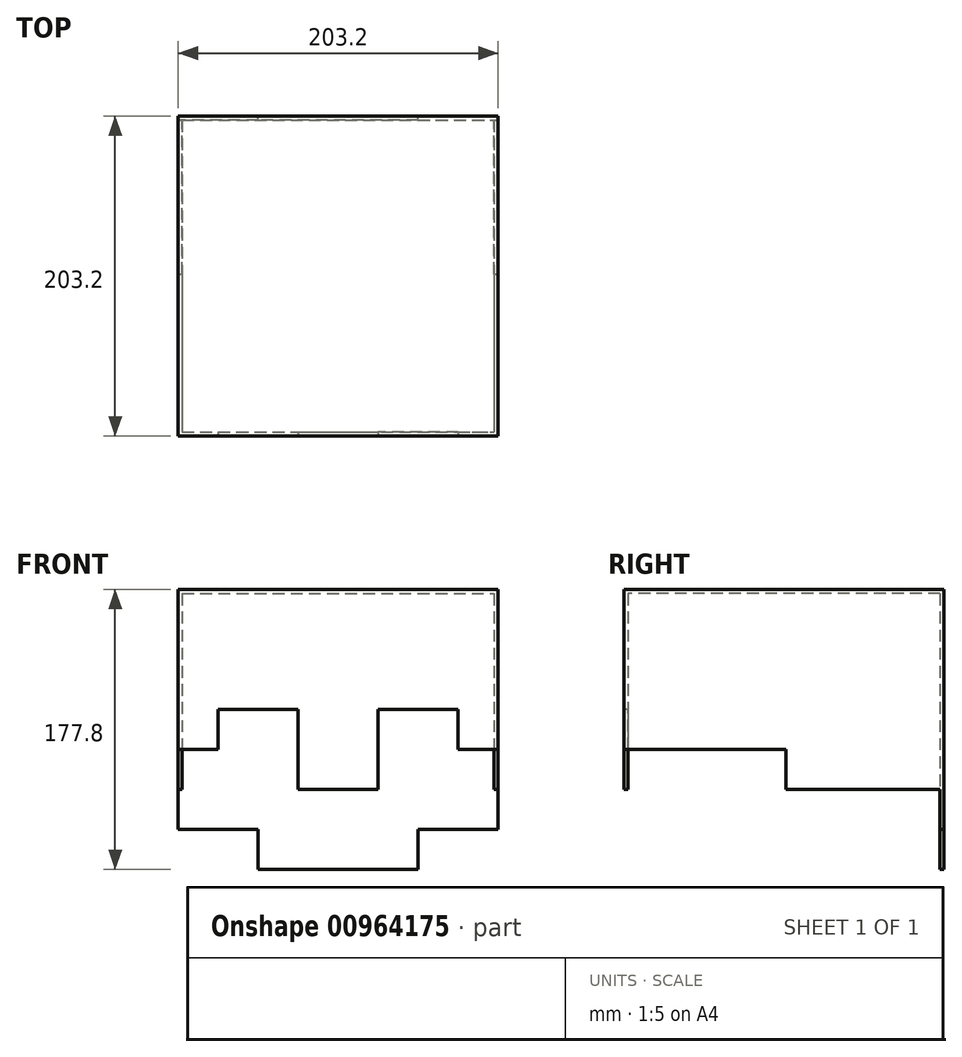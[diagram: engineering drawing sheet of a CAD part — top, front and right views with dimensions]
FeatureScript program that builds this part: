
annotation { "Feature Type Name" : "Feature", "Feature Type Description" : "" }
export const myFeature = defineFeature(function(context is Context, id is Id, definition is map)
    precondition{}
    {
        {
            var Q0;
            Q0=qCreatedBy(makeId("Top.planeOp"),FACE);
            var sketch = newSketch(context, id + "F0", { "sketchPlane" : qUnion([Q0])});
            skLineSegment(sketch, "E0.bottom", {"start": v(-101.6, 101.6) * mm, "end": v(101.6, 101.6) * mm});
            skLineSegment(sketch, "E0.top", {"start": v(-101.6, -101.6) * mm, "end": v(101.6, -101.6) * mm});
            skLineSegment(sketch, "E0.left", {"start": v(-101.6, 101.6) * mm, "end": v(-101.6, -101.6) * mm});
            skLineSegment(sketch, "E0.right", {"start": v(101.6, 101.6) * mm, "end": v(101.6, -101.6) * mm});
            skPoint(sketch, "E0.middle", {"position": v(0, 0) * mm});
            skSolve(sketch);
        }
        {
            var Q0;
            Q0=makeQuery(id+"F0.imprint","IMPRINT",FACE,{"disambiguationData":[TD([[makeQuery(id+"F0.imprint","IMPRINT",EDGE,{"derivedFrom":sQuery(id+"F0.wireOp",EDGE,"E0.bottom")}),-1.0]])]});
            extrude(context, id + "F1", {"entities" : qUnion([Q0]), "depth" : 203.2 * mm, "offsetDistance" : 25.4 * mm});
        }
        {
            var Q0;
            Q0=qCreatedBy(makeId("Top.planeOp"),FACE);
            var sketch = newSketch(context, id + "F2", { "sketchPlane" : qUnion([Q0])});
            skLineSegment(sketch, "E1.bottom", {"start": v(-99.06, 99.06) * mm, "end": v(99.06, 99.06) * mm});
            skLineSegment(sketch, "E1.top", {"start": v(-99.06, -99.06) * mm, "end": v(99.06, -99.06) * mm});
            skLineSegment(sketch, "E1.left", {"start": v(-99.06, 99.06) * mm, "end": v(-99.06, -99.06) * mm});
            skLineSegment(sketch, "E1.right", {"start": v(99.06, 99.06) * mm, "end": v(99.06, -99.06) * mm});
            skPoint(sketch, "E1.middle", {"position": v(0, 0) * mm});
            skSolve(sketch);
        }
        {
            var Q0;
            Q0=qSketchRegion(id+"F2",true);
            extrude(context, id + "F3", {"entities" : qUnion([Q0]), "operationType" : NewBodyOperationType.REMOVE, "depth" : 200.66 * mm, "offsetDistance" : 25.4 * mm});
        }
        {
            var Q0;
            Q0=makeQuery(id+"F1.opExtrude","SWEPT_FACE",FACE,{"disambiguationData":[OSD([sQuery(id+"F0.wireOp",EDGE,"E0.bottom")])]});
            cPlane(context, id + "F4", {"entities" : qUnion([Q0]), "cplaneType" : CPlaneType.OFFSET, "offset" : 0 * mm, "width" : 152.4 * mm, "height" : 152.4 * mm});
        }
        {
            var Q0;
            Q0=makeQuery(id+"F1.opExtrude","SWEPT_FACE",FACE,{"disambiguationData":[OSD([sQuery(id+"F0.wireOp",EDGE,"E0.right")])]});
            cPlane(context, id + "F5", {"entities" : qUnion([Q0]), "cplaneType" : CPlaneType.OFFSET, "offset" : 0 * mm, "width" : 152.4 * mm, "height" : 152.4 * mm});
        }
        {
            var Q0;
            Q0=qCreatedBy(id+"F5.planeOp",FACE);
            var sketch = newSketch(context, id + "F6", { "sketchPlane" : qUnion([Q0])});
            skLineSegment(sketch, "E2", {"start": v(1.27, 101.6) * mm, "end": v(-99.06, 101.6) * mm});
            skLineSegment(sketch, "E3", {"start": v(1.27, 101.6) * mm, "end": v(1.27, 76.2) * mm});
            skLineSegment(sketch, "E4", {"start": v(1.27, 76.2) * mm, "end": v(99.06, 76.2) * mm});
            skPoint(sketch, "E5.orphan", {"position": v(101.6, 101.6) * mm});
            skLineSegment(sketch, "E6", {"start": v(-99.06, 101.6) * mm, "end": v(-99.06, 0) * mm});
            skLineSegment(sketch, "E7", {"start": v(-99.06, 0) * mm, "end": v(99.06, 0) * mm});
            skLineSegment(sketch, "E8", {"start": v(99.06, 0) * mm, "end": v(99.06, 76.2) * mm});
            skSolve(sketch);
        }
        {
            var Q0;
            Q0=qSketchRegion(id+"F6",true);
            extrude(context, id + "F7", {"entities" : qUnion([Q0]), "operationType" : NewBodyOperationType.REMOVE, "endBound" : BoundingType.THROUGH_ALL, "oppositeDirection" : true, "depth" : 25.4 * mm, "offsetDistance" : 25.4 * mm});
        }
        {
            var Q0;
            Q0=makeQuery(id+"F1.opExtrude","SWEPT_FACE",FACE,{"disambiguationData":[OSD([sQuery(id+"F0.wireOp",EDGE,"E0.bottom")])]});
            cPlane(context, id + "F8", {"entities" : qUnion([Q0]), "cplaneType" : CPlaneType.OFFSET, "offset" : 0 * mm, "width" : 152.4 * mm, "height" : 152.4 * mm});
        }
        {
            var Q0;
            Q0=qCreatedBy(id+"F8.planeOp",FACE);
            var sketch = newSketch(context, id + "F9", { "sketchPlane" : qUnion([Q0])});
            skLineSegment(sketch, "E9.bottom", {"start": v(101.6, 0) * mm, "end": v(-101.6, 0) * mm});
            skLineSegment(sketch, "E9.top", {"start": v(50.8, 25.4) * mm, "end": v(-50.8, 25.4) * mm});
            skLineSegment(sketch, "E9.left", {"start": v(101.6, 0) * mm, "end": v(101.6, 25.4) * mm});
            skLineSegment(sketch, "E9.right", {"start": v(-101.6, 0) * mm, "end": v(-101.6, 25.4) * mm});
            skLineSegment(sketch, "E10.top", {"start": v(-101.6, 50.8) * mm, "end": v(-50.8, 50.8) * mm});
            skLineSegment(sketch, "E10.left", {"start": v(-101.6, 25.4) * mm, "end": v(-101.6, 50.8) * mm});
            skLineSegment(sketch, "E10.right", {"start": v(-50.8, 25.4) * mm, "end": v(-50.8, 50.8) * mm});
            skLineSegment(sketch, "E11.top", {"start": v(101.6, 50.8) * mm, "end": v(50.8, 50.8) * mm});
            skLineSegment(sketch, "E11.left", {"start": v(101.6, 25.4) * mm, "end": v(101.6, 50.8) * mm});
            skLineSegment(sketch, "E11.right", {"start": v(50.8, 25.4) * mm, "end": v(50.8, 50.8) * mm});
            skSolve(sketch);
        }
        {
            var Q0;
            Q0=qSketchRegion(id+"F9",true);
            extrude(context, id + "F10", {"entities" : qUnion([Q0]), "operationType" : NewBodyOperationType.REMOVE, "endBound" : BoundingType.UP_TO_NEXT, "oppositeDirection" : true, "depth" : 25.4 * mm, "offsetDistance" : 25.4 * mm});
        }
        {
            var Q0;
            Q0=makeQuery(id+"F1.opExtrude","SWEPT_FACE",FACE,{"disambiguationData":[OSD([sQuery(id+"F0.wireOp",EDGE,"E0.top")])]});
            cPlane(context, id + "F11", {"entities" : qUnion([Q0]), "cplaneType" : CPlaneType.OFFSET, "offset" : 0 * mm, "width" : 152.4 * mm, "height" : 152.4 * mm});
        }
        {
            var Q0;
            Q0=qCreatedBy(id+"F11.planeOp",FACE);
            var sketch = newSketch(context, id + "F12", { "sketchPlane" : qUnion([Q0])});
            skLineSegment(sketch, "E12.bottom", {"start": v(-101.6, 0) * mm, "end": v(101.6, 0) * mm});
            skLineSegment(sketch, "E12.top", {"start": v(-101.6, 101.6) * mm, "end": v(-76.2, 101.6) * mm});
            skLineSegment(sketch, "E12.left", {"start": v(-101.6, 0) * mm, "end": v(-101.6, 101.6) * mm});
            skLineSegment(sketch, "E12.right", {"start": v(101.6, 0) * mm, "end": v(101.6, 101.6) * mm});
            skLineSegment(sketch, "E13.top", {"start": v(-76.2, 127) * mm, "end": v(-25.4, 127) * mm});
            skLineSegment(sketch, "E13.left", {"start": v(-76.2, 101.6) * mm, "end": v(-76.2, 127) * mm});
            skLineSegment(sketch, "E13.right", {"start": v(-25.4, 101.6) * mm, "end": v(-25.4, 127) * mm});
            skLineSegment(sketch, "E14.top", {"start": v(76.2, 127) * mm, "end": v(25.4, 127) * mm});
            skLineSegment(sketch, "E14.left", {"start": v(76.2, 101.6) * mm, "end": v(76.2, 127) * mm});
            skLineSegment(sketch, "E14.right", {"start": v(25.4, 101.6) * mm, "end": v(25.4, 127) * mm});
            skLineSegment(sketch, "E15.top", {"start": v(-25.4, 76.2) * mm, "end": v(25.4, 76.2) * mm});
            skLineSegment(sketch, "E15.left", {"start": v(-25.4, 101.6) * mm, "end": v(-25.4, 76.2) * mm});
            skLineSegment(sketch, "E15.right", {"start": v(25.4, 101.6) * mm, "end": v(25.4, 76.2) * mm});
            skLineSegment(sketch, "E16.trimOffspring", {"start": v(76.2, 101.6) * mm, "end": v(101.6, 101.6) * mm});
            skSolve(sketch);
        }
        {
            var Q0;
            Q0=qSketchRegion(id+"F12",true);
            extrude(context, id + "F13", {"entities" : qUnion([Q0]), "operationType" : NewBodyOperationType.REMOVE, "endBound" : BoundingType.UP_TO_NEXT, "oppositeDirection" : true, "depth" : 25.4 * mm, "offsetDistance" : 25.4 * mm});
        }
    });
